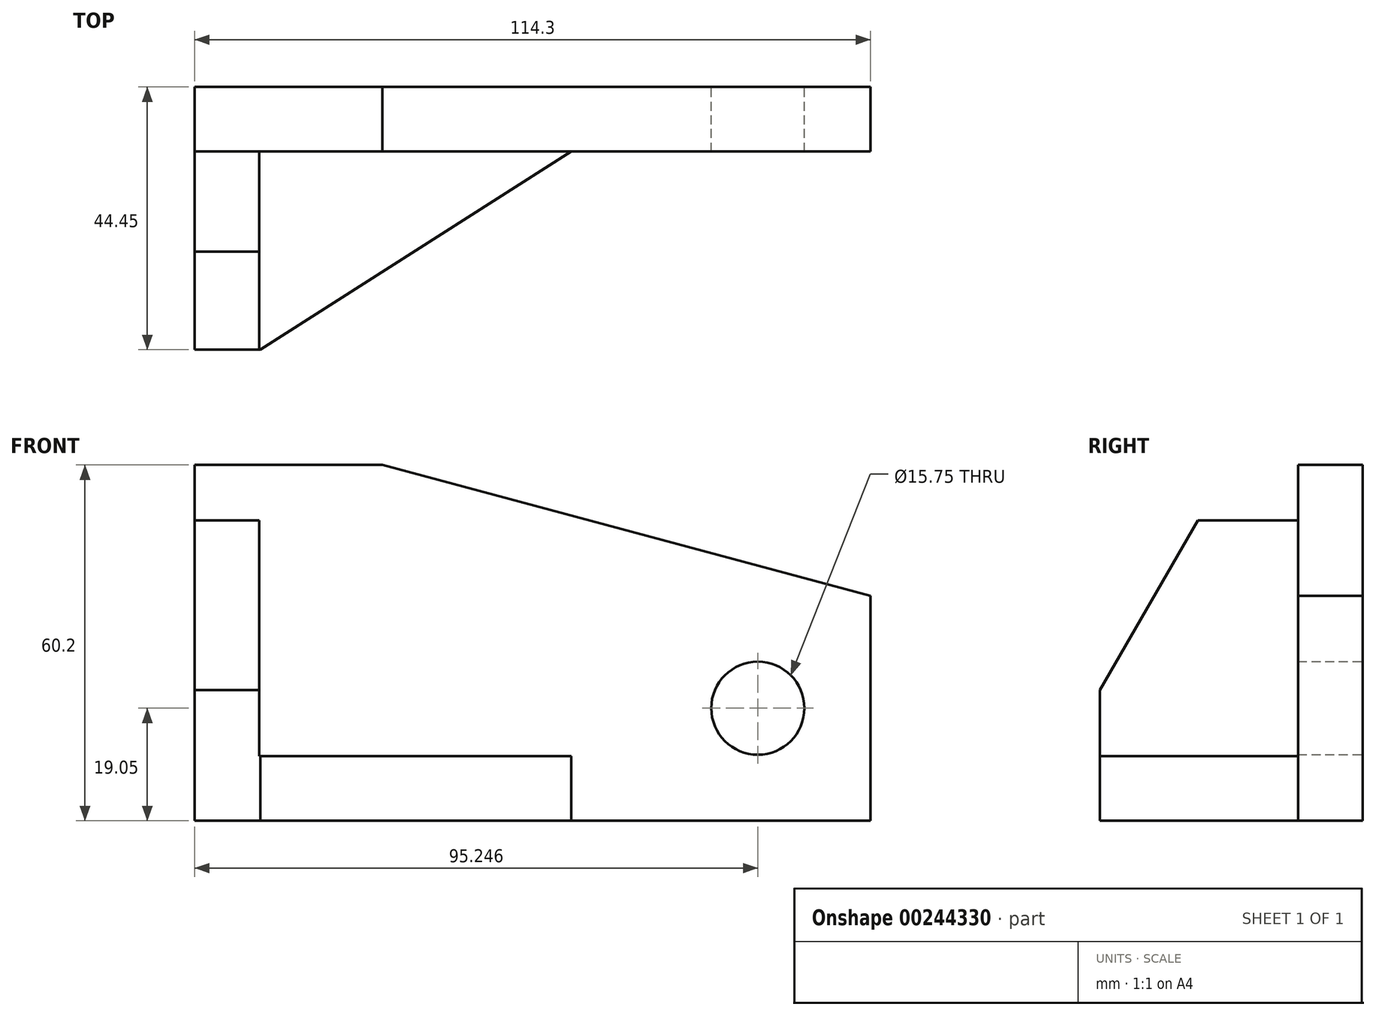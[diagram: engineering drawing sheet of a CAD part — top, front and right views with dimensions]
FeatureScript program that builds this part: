
annotation { "Feature Type Name" : "Feature", "Feature Type Description" : "" }
export const myFeature = defineFeature(function(context is Context, id is Id, definition is map)
    precondition{}
    {
        {
            var Q0;
            Q0=qCreatedBy(makeId("Front.planeOp"),FACE);
            var sketch = newSketch(context, id + "F0", { "sketchPlane" : qUnion([Q0])});
            skLineSegment(sketch, "E0", {"start": v(-45.24, 0) * mm, "end": v(69.06, 0) * mm});
            skLineSegment(sketch, "E1", {"start": v(69.06, 0) * mm, "end": v(69.06, 38.08) * mm});
            skLineSegment(sketch, "E2", {"start": v(-13.5, 60.2) * mm, "end": v(-45.24, 60.2) * mm});
            skLineSegment(sketch, "E3", {"start": v(-45.24, 60.2) * mm, "end": v(-45.24, 0) * mm});
            skLineSegment(sketch, "E4", {"start": v(-13.5, 60.2) * mm, "end": v(69.06, 60.2) * mm});
            skLineSegment(sketch, "E5", {"start": v(69.06, 60.2) * mm, "end": v(69.06, 38.08) * mm});
            skLineSegment(sketch, "E6", {"start": v(-13.5, 60.2) * mm, "end": v(69.06, 38.08) * mm});
            skLineSegment(sketch, "E7", {"start": v(69.06, 0) * mm, "end": v(50, 0) * mm});
            skLineSegment(sketch, "E8", {"start": v(69.06, 0) * mm, "end": v(69.06, 19.05) * mm});
            skLineSegment(sketch, "E9", {"start": v(50, 0) * mm, "end": v(50, 19.05) * mm});
            skSolve(sketch);
        }
        {
            var Q0;
            Q0=sQuery(id+"F0.wireOp",EDGE,"E3");
            var Q1;
            Q1=qCreatedBy(makeId("Right.planeOp"),FACE);
            cPlane(context, id + "F1", {"entities" : qUnion([Q0, Q1]), "cplaneType" : CPlaneType.LINE_ANGLE, "offset" : 25.4 * mm, "angle" : 0 * degree, "width" : 152.4 * mm, "height" : 152.4 * mm});
        }
        {
            var Q0;
            Q0=qCreatedBy(id+"F1.planeOp",FACE);
            var sketch = newSketch(context, id + "F2", { "sketchPlane" : qUnion([Q0])});
            skLineSegment(sketch, "E10", {"start": v(0, 0) * mm, "end": v(44.45, 0) * mm});
            skLineSegment(sketch, "E11", {"start": v(44.45, 0) * mm, "end": v(44.45, 22.1) * mm});
            skLineSegment(sketch, "E12", {"start": v(44.45, 50.8) * mm, "end": v(44.45, 22.1) * mm});
            skLineSegment(sketch, "E13", {"start": v(0, 50.8) * mm, "end": v(0, 0) * mm});
            skLineSegment(sketch, "E14", {"start": v(44.45, 22.1) * mm, "end": v(27.88, 50.8) * mm});
            skLineSegment(sketch, "E15", {"start": v(44.45, 50.8) * mm, "end": v(0, 50.8) * mm});
            skSolve(sketch);
        }
        {
            var Q0;
            Q0=qCreatedBy(makeId("Top.planeOp"),FACE);
            var sketch = newSketch(context, id + "F3", { "sketchPlane" : qUnion([Q0])});
            skLineSegment(sketch, "E16", {"start": v(-45.04, 0) * mm, "end": v(-45.04, -44.45) * mm});
            skLineSegment(sketch, "E17", {"start": v(-45.04, -44.45) * mm, "end": v(-34.11, -44.45) * mm});
            skLineSegment(sketch, "E18", {"start": v(18.46, 0) * mm, "end": v(18.46, -10.92) * mm});
            skLineSegment(sketch, "E19", {"start": v(-34.11, -44.45) * mm, "end": v(18.46, -10.92) * mm});
            skLineSegment(sketch, "E20", {"start": v(-45.04, 0) * mm, "end": v(18.46, 0) * mm});
            skSolve(sketch);
        }
        {
            var Q0;
            Q0=makeQuery(id+"F0.imprint","IMPRINT",FACE,{"disambiguationData":[TD([[makeQuery(id+"F0.imprint","IMPRINT",EDGE,{"derivedFrom":sQuery(id+"F0.wireOp",EDGE,"E0")}),1.0]])]});
            extrude(context, id + "F4", {"entities" : qUnion([Q0]), "depth" : 10.92 * mm});
        }
        {
            var Q0;
            Q0=makeQuery(id+"F2.imprint","IMPRINT",FACE,{"disambiguationData":[TD([[makeQuery(id+"F2.imprint","IMPRINT",EDGE,{"derivedFrom":sQuery(id+"F2.wireOp",EDGE,"E10")}),1.0]])]});
            extrude(context, id + "F5", {"entities" : qUnion([Q0]), "operationType" : NewBodyOperationType.ADD, "oppositeDirection" : true, "depth" : 10.92 * mm});
        }
        {
            var Q0;
            {var subQ0=sQuery(id+"F3.wireOp",EDGE,"E19");Q0=makeQuery(id+"F3.imprint","IMPRINT",FACE,{"disambiguationData":[TD([[makeQuery(id+"F3.imprint","IMPRINT",EDGE,{"derivedFrom":subQ0}),1.0]])]});}
            extrude(context, id + "F6", {"entities" : qUnion([Q0]), "operationType" : NewBodyOperationType.ADD, "depth" : 10.92 * mm});
        }
        {
            var Q0;
            Q0=sQuery(id+"F0.wireOp",VERTEX,"E9.end");
            var Q1;
            Q1=makeQuery(id+"F4.opExtrude","SWEPT_BODY",BODY,{"disambiguationData":[OSD([sQuery(id+"F0.wireOp",EDGE,"E0"),sQuery(id+"F0.wireOp",EDGE,"E1"),sQuery(id+"F0.wireOp",EDGE,"E2"),sQuery(id+"F0.wireOp",EDGE,"E3"),sQuery(id+"F0.wireOp",EDGE,"E6"),sQuery(id+"F0.wireOp",EDGE,"E7"),sQuery(id+"F0.wireOp",EDGE,"E8")])]});
            hole(context, id + "F7", {"style" : HoleStyle.SIMPLE, "endStyle" : HoleEndStyle.THROUGH, "oppositeDirection" : true, "holeDiameter" : 15.75 * mm, "locations" : qUnion([Q0]), "scope" : qUnion([Q1]), "isTappedThrough" : true});
        }
    });
